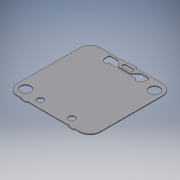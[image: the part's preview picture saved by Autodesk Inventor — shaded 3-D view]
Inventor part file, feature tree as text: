
AUTODESK INVENTOR PART (.ipt)
format: ipt  version: 2016 SP2 (Build 200236200, 236)  size: 197,120 bytes
history: native  units: mm
features: reference x16, extrude x1, fillet x1, sketch x1
ambient origin geometry x8: Origin, YZ Plane, XZ Plane, XY Plane, X Axis, Y Axis, Z Axis, Center Point
bodies: Volumenkörper1 (feature_tree)
feature tree (19):
  extrude  "Extrusion1"  Depth=6.0mm
  fillet  "Rundung1"  Radius=0.3mm
  sketch  "Skizze1"  dims[d0=0.1mm d1=0.3mm d2=0.3mm d3=0.3mm d4=0.3mm d5=0.3mm d6=0.3mm d7=0.3mm d8=0.3mm d9=0.3mm d10=135.0deg d11=1.5mm d12=2.0mm d13=8.0mm d14=8.0mm d15=12.0mm d17=2.0mm d18=10.0mm d19=1.0mm d20=2.0mm d21=3.0mm d22=2.0mm d23=0.8mm d24=0.0mm d25=1.0mm d26=1.0mm d27=1.0mm d28=6.0mm d29=6.0mm d30=6.0mm d31=6.0mm]
  reference  "Referenz1"
  reference  "Referenz2"
  reference  "Referenz3"
  reference  "Referenz4"
  reference  "Referenz5"
  reference  "Referenz6"
  reference  "Referenz7"
  reference  "Referenz8"
  reference  "Referenz9"
  reference  "Referenz10"
  reference  "Referenz11"
  reference  "Referenz12"
  reference  "Referenz13"
  reference  "Referenz14"
  reference  "Referenz15"
  reference  "Referenz16"
